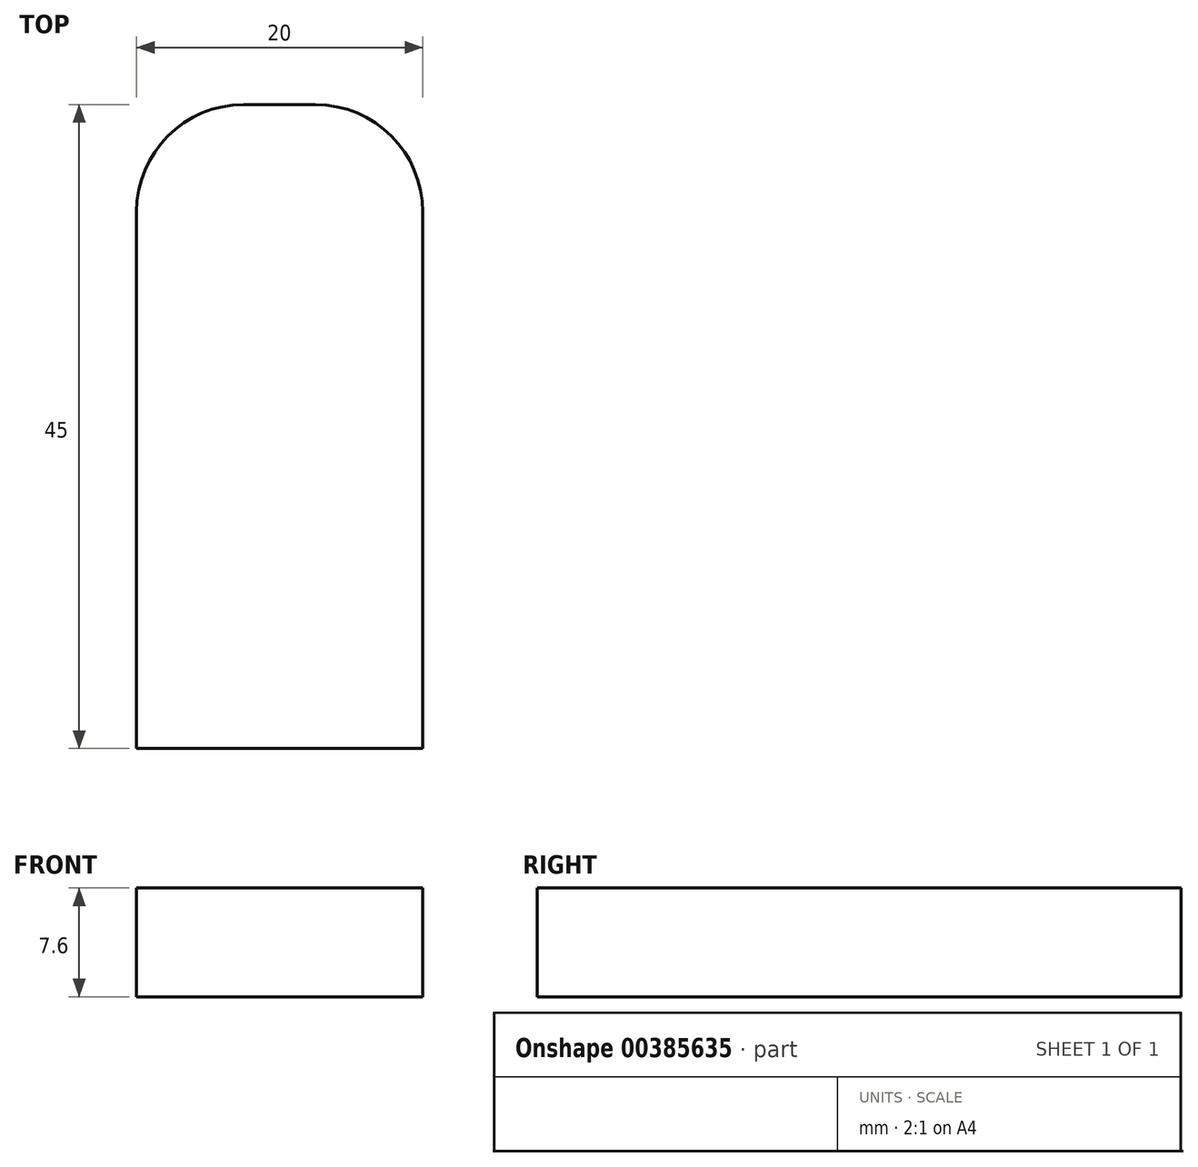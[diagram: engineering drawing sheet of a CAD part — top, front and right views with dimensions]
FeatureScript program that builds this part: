
annotation { "Feature Type Name" : "Feature", "Feature Type Description" : "" }
export const myFeature = defineFeature(function(context is Context, id is Id, definition is map)
    precondition{}
    {
        {
            var Q0;
            Q0=qCreatedBy(makeId("Top.planeOp"),FACE);
            var sketch = newSketch(context, id + "F0", { "sketchPlane" : qUnion([Q0])});
            skLineSegment(sketch, "E0.bottom", {"start": v(0, 0) * mm, "end": v(20, 0) * mm});
            skLineSegment(sketch, "E0.top", {"start": v(0, 45) * mm, "end": v(20, 45) * mm});
            skLineSegment(sketch, "E0.left", {"start": v(0, 0) * mm, "end": v(0, 45) * mm});
            skLineSegment(sketch, "E0.right", {"start": v(20, 0) * mm, "end": v(20, 45) * mm});
            skPoint(sketch, "E1", {"position": v(10, 0) * mm});
            skLineSegment(sketch, "E2", {"start": v(10, 0) * mm, "end": v(10, 16.52) * mm});
            skSolve(sketch);
        }
        {
            var Q0;
            Q0 = qSketchRegion(id + "F0", true);
            extrude(context, id + "F1", {"entities" : qUnion([Q0]), "depth" : 3.8 * mm, "hasSecondDirection" : true, "secondDirectionOppositeDirection" : true, "secondDirectionDepth" : 3.8 * mm});
        }
        {
            var Q0;
            Q0=makeQuery(id+"F1.opExtrude","SWEPT_EDGE",EDGE,{"disambiguationData":[OSD([sQuery(id+"F0.wireOp",EDGE,"E0.top"),sQuery(id+"F0.wireOp",EDGE,"E0.right")])]});
            var Q1;
            Q1=makeQuery(id+"F1.opExtrude","SWEPT_EDGE",EDGE,{"disambiguationData":[OSD([sQuery(id+"F0.wireOp",EDGE,"E0.top"),sQuery(id+"F0.wireOp",EDGE,"E0.left")])]});
            fillet(context, id + "F2", {"entities" : qUnion([Q0, Q1]), "radius" : 7.5 * mm, "tangentPropagation" : true, "allowEdgeOverflow" : false});
        }
    });
